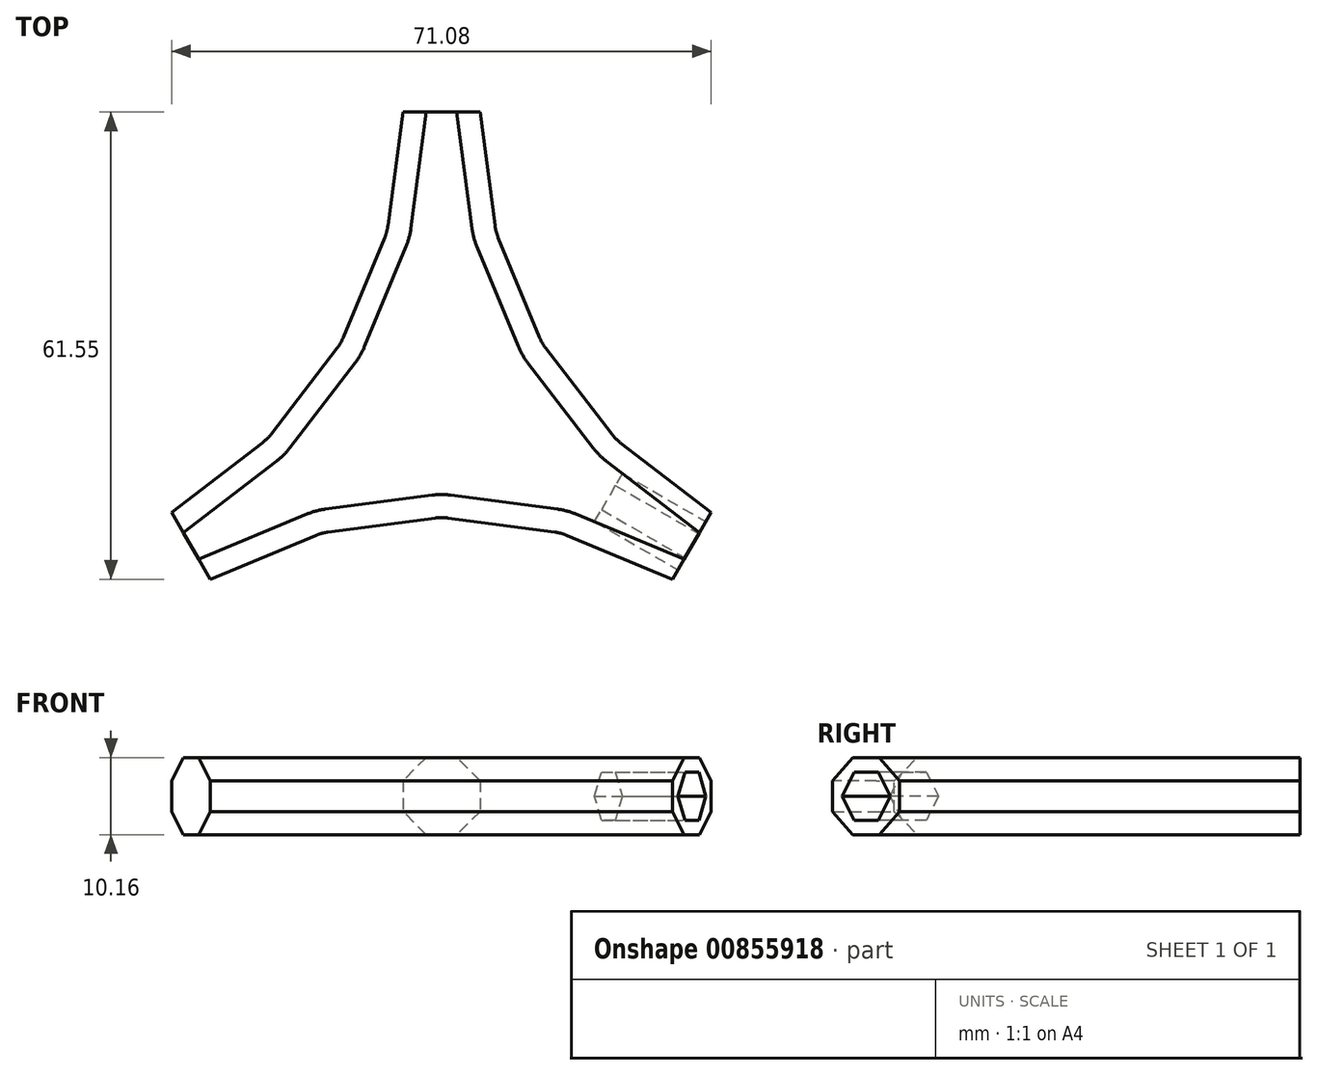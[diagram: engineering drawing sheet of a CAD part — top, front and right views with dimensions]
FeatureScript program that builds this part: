
annotation { "Feature Type Name" : "Feature", "Feature Type Description" : "" }
export const myFeature = defineFeature(function(context is Context, id is Id, definition is map)
    precondition{}
    {
        {
            var Q0;
            Q0=qCreatedBy(makeId("Top.planeOp"),FACE);
            var sketch = newSketch(context, id + "F0", { "sketchPlane" : qUnion([Q0])});
            skCircle(sketch, "E0.cCircle", {"center": v(0, 0) * mm, "radius": 44 * mm, "construction": true});
            skLineSegment(sketch, "E0.0", {"start": v(44, 0) * mm, "end": v(22, -38.1) * mm});
            skLineSegment(sketch, "E0.1", {"start": v(22, -38.1) * mm, "end": v(-22, -38.1) * mm});
            skLineSegment(sketch, "E0.2", {"start": v(-22, -38.1) * mm, "end": v(-44, 0) * mm});
            skLineSegment(sketch, "E0.3", {"start": v(-44, 0) * mm, "end": v(-22, 38.1) * mm});
            skLineSegment(sketch, "E0.4", {"start": v(-22, 38.1) * mm, "end": v(22, 38.1) * mm});
            skLineSegment(sketch, "E0.5", {"start": v(22, 38.1) * mm, "end": v(44, 0) * mm});
            skLineSegment(sketch, "E1", {"start": v(-33, -19.05) * mm, "end": v(0, 0) * mm});
            skLineSegment(sketch, "E2", {"start": v(33, -19.05) * mm, "end": v(0, 0) * mm});
            skLineSegment(sketch, "E3", {"start": v(0, 38.1) * mm, "end": v(0, 0) * mm});
            skSolve(sketch);
        }
        {
            var Q0;
            Q0=qCreatedBy(makeId("Top.planeOp"),FACE);
            var sketch = newSketch(context, id + "F1", { "sketchPlane" : qUnion([Q0])});
            skArc(sketch, "E4", {"start": v(5.08, 38.1) * mm, "mid": v(13.24, 7.64) * mm, "end": v(35.54, -14.65) * mm});
            skLineSegment(sketch, "E5", {"start": v(33, -19.05) * mm, "end": v(0, 0) * mm, "construction": true});
            skArc(sketch, "E6.MirrorCS", {"start": v(-30.46, -23.45) * mm, "mid": v(0, -15.29) * mm, "end": v(30.46, -23.45) * mm});
            skArc(sketch, "E7.MirrorCS", {"start": v(-35.54, -14.65) * mm, "mid": v(-13.24, 7.64) * mm, "end": v(-5.08, 38.1) * mm});
            skSolve(sketch);
        }
        {
            var Q0;
            Q0=qCreatedBy(makeId("Top.planeOp"),FACE);
            var sketch = newSketch(context, id + "F2", { "sketchPlane" : qUnion([Q0])});
            skLineSegment(sketch, "E8", {"start": v(5.08, 38.1) * mm, "end": v(7.16, 22.34) * mm});
            skLineSegment(sketch, "E9", {"start": v(7.16, 22.34) * mm, "end": v(13.24, 7.64) * mm});
            skLineSegment(sketch, "E10", {"start": v(13.24, 7.64) * mm, "end": v(22.92, -4.97) * mm});
            skLineSegment(sketch, "E11.MirrorCS", {"start": v(0, -15.29) * mm, "end": v(15.76, -17.36) * mm});
            skLineSegment(sketch, "E12.MirrorCS", {"start": v(-15.76, -17.36) * mm, "end": v(0, -15.29) * mm});
            skLineSegment(sketch, "E13.MirrorCS", {"start": v(-30.46, -23.45) * mm, "end": v(-15.76, -17.36) * mm});
            skLineSegment(sketch, "E14.MirrorCS", {"start": v(-35.54, -14.65) * mm, "end": v(-22.92, -4.97) * mm});
            skLineSegment(sketch, "E15.MirrorCS", {"start": v(-22.92, -4.97) * mm, "end": v(-13.24, 7.64) * mm});
            skLineSegment(sketch, "E16.MirrorCS", {"start": v(-13.24, 7.64) * mm, "end": v(-7.16, 22.34) * mm});
            skLineSegment(sketch, "E17", {"start": v(-35.54, -14.65) * mm, "end": v(-30.46, -23.45) * mm});
            skLineSegment(sketch, "E18", {"start": v(22.92, -4.97) * mm, "end": v(35.54, -14.65) * mm});
            skLineSegment(sketch, "E19", {"start": v(-7.16, 22.34) * mm, "end": v(-5.08, 38.1) * mm});
            skLineSegment(sketch, "E20", {"start": v(-5.08, 38.1) * mm, "end": v(5.08, 38.1) * mm});
            skLineSegment(sketch, "E21", {"start": v(15.76, -17.36) * mm, "end": v(30.46, -23.45) * mm});
            skLineSegment(sketch, "E22", {"start": v(30.46, -23.45) * mm, "end": v(35.54, -14.65) * mm});
            skSolve(sketch);
        }
        {
            var Q0;
            Q0 = qSketchRegion(id + "F2", true);
            extrude(context, id + "F3", {"entities" : qUnion([Q0]), "endBound" : BoundingType.SYMMETRIC, "depth" : 10.16 * mm, "offsetDistance" : 25.4 * mm});
        }
        {
            var Q0;
            Q0=makeQuery(id+"F3.opExtrude","SWEPT_EDGE",EDGE,{"disambiguationData":[OSD([sQuery(id+"F2.wireOp",EDGE,"E14.MirrorCS"),sQuery(id+"F2.wireOp",EDGE,"E15.MirrorCS")])]});
            var Q1;
            Q1=makeQuery(id+"F3.opExtrude","SWEPT_EDGE",EDGE,{"disambiguationData":[OSD([sQuery(id+"F2.wireOp",EDGE,"E15.MirrorCS"),sQuery(id+"F2.wireOp",EDGE,"E16.MirrorCS")])]});
            var Q2;
            Q2=makeQuery(id+"F3.opExtrude","SWEPT_EDGE",EDGE,{"disambiguationData":[OSD([sQuery(id+"F2.wireOp",EDGE,"E8"),sQuery(id+"F2.wireOp",EDGE,"E9")])]});
            var Q3;
            Q3=makeQuery(id+"F3.opExtrude","SWEPT_EDGE",EDGE,{"disambiguationData":[OSD([sQuery(id+"F2.wireOp",EDGE,"E9"),sQuery(id+"F2.wireOp",EDGE,"E10")])]});
            var Q4;
            Q4=makeQuery(id+"F3.opExtrude","SWEPT_EDGE",EDGE,{"disambiguationData":[OSD([sQuery(id+"F2.wireOp",EDGE,"E12.MirrorCS"),sQuery(id+"F2.wireOp",EDGE,"E13.MirrorCS")])]});
            var Q5;
            Q5=makeQuery(id+"F3.opExtrude","SWEPT_EDGE",EDGE,{"disambiguationData":[OSD([sQuery(id+"F2.wireOp",EDGE,"E11.MirrorCS"),sQuery(id+"F2.wireOp",EDGE,"E12.MirrorCS")])]});
            var Q6;
            Q6=makeQuery(id+"F3.opExtrude","SWEPT_EDGE",EDGE,{"disambiguationData":[OSD([sQuery(id+"F2.wireOp",EDGE,"E10"),sQuery(id+"F2.wireOp",EDGE,"E18")])]});
            var Q7;
            Q7=makeQuery(id+"F3.opExtrude","SWEPT_EDGE",EDGE,{"disambiguationData":[OSD([sQuery(id+"F2.wireOp",EDGE,"E16.MirrorCS"),sQuery(id+"F2.wireOp",EDGE,"E19")])]});
            var Q8;
            Q8=makeQuery(id+"F3.opExtrude","SWEPT_EDGE",EDGE,{"disambiguationData":[OSD([sQuery(id+"F2.wireOp",EDGE,"E11.MirrorCS"),sQuery(id+"F2.wireOp",EDGE,"E21")])]});
            fillet(context, id + "F4", {"entities" : qUnion([Q0, Q1, Q2, Q3, Q4, Q5, Q6, Q7, Q8]), "radius" : 6.35 * mm, "tangentPropagation" : true, "allowEdgeOverflow" : false});
        }
        {
            var Q0;
            Q0=makeQuery(id+"F3.opExtrude","CAP_EDGE",EDGE,{"disambiguationData":[OSD([sQuery(id+"F2.wireOp",EDGE,"E13.MirrorCS")])],"isStart":false});
            var Q1;
            Q1=makeQuery(id+"F3.opExtrude","CAP_EDGE",EDGE,{"disambiguationData":[OSD([sQuery(id+"F2.wireOp",EDGE,"E12.MirrorCS")])],"isStart":false});
            var Q2;
            Q2=makeQuery(id+"F3.opExtrude","CAP_EDGE",EDGE,{"disambiguationData":[OSD([sQuery(id+"F2.wireOp",EDGE,"E11.MirrorCS")])],"isStart":false});
            var Q3;
            Q3=makeQuery(id+"F3.opExtrude","CAP_EDGE",EDGE,{"disambiguationData":[OSD([sQuery(id+"F2.wireOp",EDGE,"E14.MirrorCS")])],"isStart":false});
            var Q4;
            Q4=makeQuery(id+"F3.opExtrude","CAP_EDGE",EDGE,{"disambiguationData":[OSD([sQuery(id+"F2.wireOp",EDGE,"E15.MirrorCS")])],"isStart":false});
            var Q5;
            Q5=makeQuery(id+"F3.opExtrude","CAP_EDGE",EDGE,{"disambiguationData":[OSD([sQuery(id+"F2.wireOp",EDGE,"E16.MirrorCS")])],"isStart":false});
            var Q6;
            Q6=makeQuery(id+"F3.opExtrude","CAP_EDGE",EDGE,{"disambiguationData":[OSD([sQuery(id+"F2.wireOp",EDGE,"E8")])],"isStart":false});
            var Q7;
            Q7=makeQuery(id+"F3.opExtrude","CAP_EDGE",EDGE,{"disambiguationData":[OSD([sQuery(id+"F2.wireOp",EDGE,"E9")])],"isStart":false});
            var Q8;
            Q8=makeQuery(id+"F3.opExtrude","CAP_EDGE",EDGE,{"disambiguationData":[OSD([sQuery(id+"F2.wireOp",EDGE,"E10")])],"isStart":false});
            var Q9;
            Q9=makeQuery(id+"F3.opExtrude","CAP_EDGE",EDGE,{"disambiguationData":[OSD([sQuery(id+"F2.wireOp",EDGE,"E14.MirrorCS")])],"isStart":true});
            var Q10;
            Q10=makeQuery(id+"F3.opExtrude","CAP_EDGE",EDGE,{"disambiguationData":[OSD([sQuery(id+"F2.wireOp",EDGE,"E15.MirrorCS")])],"isStart":true});
            var Q11;
            Q11=makeQuery(id+"F3.opExtrude","CAP_EDGE",EDGE,{"disambiguationData":[OSD([sQuery(id+"F2.wireOp",EDGE,"E16.MirrorCS")])],"isStart":true});
            var Q12;
            Q12=makeQuery(id+"F3.opExtrude","CAP_EDGE",EDGE,{"disambiguationData":[OSD([sQuery(id+"F2.wireOp",EDGE,"E8")])],"isStart":true});
            var Q13;
            Q13=makeQuery(id+"F3.opExtrude","CAP_EDGE",EDGE,{"disambiguationData":[OSD([sQuery(id+"F2.wireOp",EDGE,"E9")])],"isStart":true});
            var Q14;
            Q14=makeQuery(id+"F3.opExtrude","CAP_EDGE",EDGE,{"disambiguationData":[OSD([sQuery(id+"F2.wireOp",EDGE,"E10")])],"isStart":true});
            var Q15;
            Q15=makeQuery(id+"F3.opExtrude","CAP_EDGE",EDGE,{"disambiguationData":[OSD([sQuery(id+"F2.wireOp",EDGE,"E11.MirrorCS")])],"isStart":true});
            var Q16;
            Q16=makeQuery(id+"F3.opExtrude","CAP_EDGE",EDGE,{"disambiguationData":[OSD([sQuery(id+"F2.wireOp",EDGE,"E12.MirrorCS")])],"isStart":true});
            var Q17;
            Q17=makeQuery(id+"F3.opExtrude","CAP_EDGE",EDGE,{"disambiguationData":[OSD([sQuery(id+"F2.wireOp",EDGE,"E13.MirrorCS")])],"isStart":true});
            chamfer(context, id + "F5", {"entities" : qUnion([Q0, Q1, Q2, Q3, Q4, Q5, Q6, Q7, Q8, Q9, Q10, Q11, Q12, Q13, Q14, Q15, Q16, Q17]), "width" : 3.05 * mm, "tangentPropagation" : true});
        }
        {
            var Q0;
            Q0=makeQuery(id+"F3.opExtrude","SWEPT_FACE",FACE,{"disambiguationData":[OSD([sQuery(id+"F2.wireOp",EDGE,"E22")])]});
            var sketch = newSketch(context, id + "F6", { "sketchPlane" : qUnion([Q0])});
            skCircle(sketch, "E23.cCircle", {"center": v(0, 0) * mm, "radius": 3.67 * mm, "construction": true});
            skLineSegment(sketch, "E23.0", {"start": v(-3.67, 0) * mm, "end": v(-1.83, 3.17) * mm});
            skLineSegment(sketch, "E23.1", {"start": v(-1.83, 3.18) * mm, "end": v(1.83, 3.18) * mm});
            skLineSegment(sketch, "E23.2", {"start": v(1.83, 3.17) * mm, "end": v(3.67, 0) * mm});
            skLineSegment(sketch, "E23.3", {"start": v(3.67, 0) * mm, "end": v(1.83, -3.17) * mm});
            skLineSegment(sketch, "E23.4", {"start": v(1.83, -3.17) * mm, "end": v(-1.83, -3.18) * mm});
            skLineSegment(sketch, "E23.5", {"start": v(-1.83, -3.18) * mm, "end": v(-3.67, 0) * mm});
            skSolve(sketch);
        }
        {
            var Q0;
            Q0 = qSketchRegion(id + "F6", true);
            extrude(context, id + "F7", {"entities" : qUnion([Q0]), "operationType" : NewBodyOperationType.REMOVE, "oppositeDirection" : true, "depth" : 12.7 * mm, "offsetDistance" : 25.4 * mm});
        }
        {
            var Q0;
            Q0=qCreatedBy(makeId("Front.planeOp"),FACE);
            var sketch = newSketch(context, id + "F8", { "sketchPlane" : qUnion([Q0])});
            skLineSegment(sketch, "E24", {"start": v(0, -47.3) * mm, "end": v(0, 39.17) * mm});
            skSolve(sketch);
        }
    });
